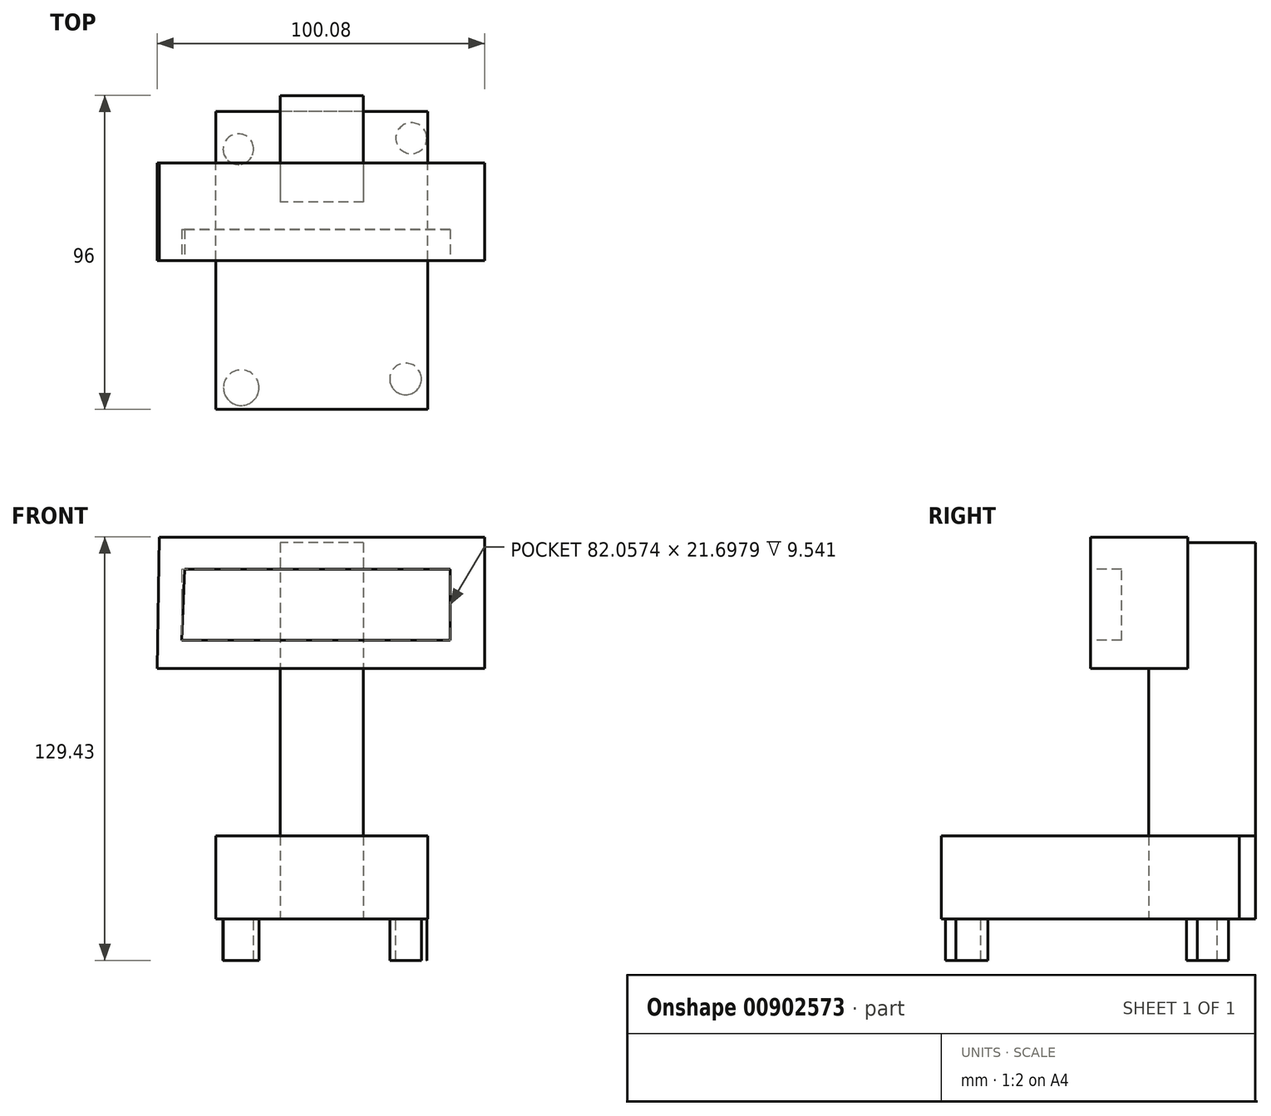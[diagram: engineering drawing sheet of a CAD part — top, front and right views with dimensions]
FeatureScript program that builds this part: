
annotation { "Feature Type Name" : "Feature", "Feature Type Description" : "" }
export const myFeature = defineFeature(function(context is Context, id is Id, definition is map)
    precondition{}
    {
        {
            var Q0;
            Q0=qCreatedBy(makeId("Top.planeOp"),FACE);
            var sketch = newSketch(context, id + "F0", { "sketchPlane" : qUnion([Q0])});
            skLineSegment(sketch, "E0.bottom", {"start": v(32.35, -45.54) * mm, "end": v(-32.35, -45.54) * mm});
            skLineSegment(sketch, "E0.top", {"start": v(32.35, 45.54) * mm, "end": v(-32.35, 45.54) * mm});
            skLineSegment(sketch, "E0.left", {"start": v(32.35, -45.54) * mm, "end": v(32.35, 45.54) * mm});
            skLineSegment(sketch, "E0.right", {"start": v(-32.35, -45.54) * mm, "end": v(-32.35, 45.54) * mm});
            skPoint(sketch, "E0.middle", {"position": v(0, 0) * mm});
            skSolve(sketch);
        }
        {
            var Q0;
            Q0=qCreatedBy(makeId("Top.planeOp"),FACE);
            var sketch = newSketch(context, id + "F1", { "sketchPlane" : qUnion([Q0])});
            skLineSegment(sketch, "E1.bottom", {"start": v(12.72, 75.86) * mm, "end": v(-12.72, 75.86) * mm});
            skLineSegment(sketch, "E1.top", {"start": v(12.72, 17.84) * mm, "end": v(-12.72, 17.84) * mm});
            skLineSegment(sketch, "E1.left", {"start": v(12.72, 75.86) * mm, "end": v(12.72, 17.84) * mm});
            skLineSegment(sketch, "E1.right", {"start": v(-12.72, 75.86) * mm, "end": v(-12.72, 17.84) * mm});
            skPoint(sketch, "E1.middle", {"position": v(0, 46.85) * mm});
            skSolve(sketch);
        }
        {
            var Q0;
            Q0=makeQuery(id+"F0.imprint","IMPRINT",FACE,{"disambiguationData":[TD([[makeQuery(id+"F0.imprint","IMPRINT",EDGE,{"derivedFrom":sQuery(id+"F0.wireOp",EDGE,"E0.bottom")}),-1.0]])]});
            var Q1;
            Q1 = qSketchRegion(id + "F1", true);
            extrude(context, id + "F2", {"entities" : qUnion([Q0, Q1]), "depth" : 25.4 * mm, "offsetDistance" : 25.4 * mm});
        }
        {
            var Q0;
            Q0=makeQuery(id+"F2.opExtrude","CAP_FACE",FACE,{"disambiguationData":[OSD([sQuery(id+"F1.wireOp",EDGE,"E1.bottom"),sQuery(id+"F1.wireOp",EDGE,"E1.top"),sQuery(id+"F1.wireOp",EDGE,"E1.left"),sQuery(id+"F1.wireOp",EDGE,"E1.right")])],"isStart":false});
            extrude(context, id + "F3", {"entities" : qUnion([Q0]), "depth" : 89.6 * mm, "offsetDistance" : 25.4 * mm});
        }
        {
            var Q0;
            Q0=makeQuery(id+"F2.opExtrude","CAP_FACE",FACE,{"disambiguationData":[OSD([sQuery(id+"F0.wireOp",EDGE,"E0.bottom"),sQuery(id+"F0.wireOp",EDGE,"E0.top"),sQuery(id+"F0.wireOp",EDGE,"E0.left"),sQuery(id+"F0.wireOp",EDGE,"E0.right")])],"isStart":true});
            var sketch = newSketch(context, id + "F4", { "sketchPlane" : qUnion([Q0])});
            skSolve(sketch);
        }
        {
            var Q0;
            Q0=makeQuery(id+"F4.imprint","IMPRINT",FACE,{"disambiguationData":[TD([[makeQuery(id+"F4.imprint","IMPRINT",EDGE,{"derivedFrom":makeQuery(id+"F2.opExtrude","CAP_EDGE",EDGE,{"disambiguationData":[OSD([sQuery(id+"F0.wireOp",EDGE,"E0.bottom")])],"isStart":true})}),1.0]])]});
            var sketch = newSketch(context, id + "F5", { "sketchPlane" : qUnion([Q0])});
            skCircle(sketch, "E2", {"center": v(27.35, -37.41) * mm, "radius": 4.73 * mm});
            skCircle(sketch, "E3", {"center": v(25.62, 36.22) * mm, "radius": 4.84 * mm});
            skCircle(sketch, "E4", {"center": v(-25.5, -34.05) * mm, "radius": 4.69 * mm});
            skCircle(sketch, "E5", {"center": v(-24.62, 38.89) * mm, "radius": 5.44 * mm});
            skSolve(sketch);
        }
        {
            var Q0;
            Q0 = qSketchRegion(id + "F5", true);
            extrude(context, id + "F6", {"entities" : qUnion([Q0]), "operationType" : NewBodyOperationType.ADD, "depth" : 12.7 * mm, "offsetDistance" : 25.4 * mm});
        }
        {
            var Q0;
            Q0=qCreatedBy(makeId("Front.planeOp"),FACE);
            var sketch = newSketch(context, id + "F7", { "sketchPlane" : qUnion([Q0])});
            skLineSegment(sketch, "E6", {"start": v(-49.7, 116.73) * mm, "end": v(49.78, 116.73) * mm});
            skLineSegment(sketch, "E7", {"start": v(49.78, 116.73) * mm, "end": v(49.78, 76.5) * mm});
            skLineSegment(sketch, "E8", {"start": v(49.78, 76.5) * mm, "end": v(-50.3, 76.5) * mm});
            skLineSegment(sketch, "E9", {"start": v(-50.3, 76.5) * mm, "end": v(-49.7, 116.73) * mm});
            skSolve(sketch);
        }
        {
            var Q0;
            Q0=makeQuery(id+"F7.imprint","IMPRINT",FACE,{"disambiguationData":[TD([[makeQuery(id+"F7.imprint","IMPRINT",EDGE,{"derivedFrom":sQuery(id+"F7.wireOp",EDGE,"E6")}),-1.0]])]});
            extrude(context, id + "F8", {"entities" : qUnion([Q0]), "operationType" : NewBodyOperationType.ADD, "oppositeDirection" : true, "depth" : 29.76 * mm, "offsetDistance" : 25.4 * mm});
        }
        {
            var Q0;
            Q0=makeQuery(id+"F3.opExtrude","SWEPT_FACE",FACE,{"disambiguationData":[OSD([sQuery(id+"F1.wireOp",EDGE,"E1.bottom")])]});
            extrude(context, id + "F9", {"entities" : qUnion([Q0]), "operationType" : NewBodyOperationType.REMOVE, "oppositeDirection" : true, "depth" : 25.4 * mm, "offsetDistance" : 25.4 * mm});
        }
        {
            var Q0;
            Q0=makeQuery(id+"F2.opExtrude","SWEPT_FACE",FACE,{"disambiguationData":[OSD([sQuery(id+"F1.wireOp",EDGE,"E1.bottom")])]});
            extrude(context, id + "F10", {"entities" : qUnion([Q0]), "operationType" : NewBodyOperationType.REMOVE, "oppositeDirection" : true, "depth" : 25.4 * mm, "offsetDistance" : 25.4 * mm});
        }
        {
            var Q0;
            Q0=makeQuery(id+"F8.opExtrude","CAP_FACE",FACE,{"disambiguationData":[OSD([sQuery(id+"F7.wireOp",EDGE,"E6"),sQuery(id+"F7.wireOp",EDGE,"E7"),sQuery(id+"F7.wireOp",EDGE,"E8"),sQuery(id+"F7.wireOp",EDGE,"E9")])],"isStart":true});
            var sketch = newSketch(context, id + "F11", { "sketchPlane" : qUnion([Q0])});
            skLineSegment(sketch, "E10", {"start": v(-41.92, 106.85) * mm, "end": v(39.22, 106.85) * mm});
            skLineSegment(sketch, "E11", {"start": v(39.22, 106.85) * mm, "end": v(39.22, 85.15) * mm});
            skLineSegment(sketch, "E12", {"start": v(39.22, 85.15) * mm, "end": v(-42.84, 85.15) * mm});
            skLineSegment(sketch, "E13", {"start": v(-42.84, 85.15) * mm, "end": v(-41.92, 106.85) * mm});
            skSolve(sketch);
        }
        {
            var Q0;
            Q0=makeQuery(id+"F11.imprint","IMPRINT",FACE,{"disambiguationData":[TD([[makeQuery(id+"F11.imprint","IMPRINT",EDGE,{"derivedFrom":sQuery(id+"F11.wireOp",EDGE,"E10")}),-1.0]])]});
            extrude(context, id + "F12", {"entities" : qUnion([Q0]), "operationType" : NewBodyOperationType.ADD, "depth" : 25.4 * mm, "offsetDistance" : 25.4 * mm});
        }
        {
            var Q0;
            Q0=makeQuery(id+"F12.opExtrude","CAP_FACE",FACE,{"disambiguationData":[OSD([sQuery(id+"F11.wireOp",EDGE,"E10"),sQuery(id+"F11.wireOp",EDGE,"E11"),sQuery(id+"F11.wireOp",EDGE,"E12"),sQuery(id+"F11.wireOp",EDGE,"E13")])],"isStart":false});
            extrude(context, id + "F13", {"entities" : qUnion([Q0]), "operationType" : NewBodyOperationType.REMOVE, "oppositeDirection" : true, "depth" : 34.94 * mm, "offsetDistance" : 25.4 * mm});
        }
    });
